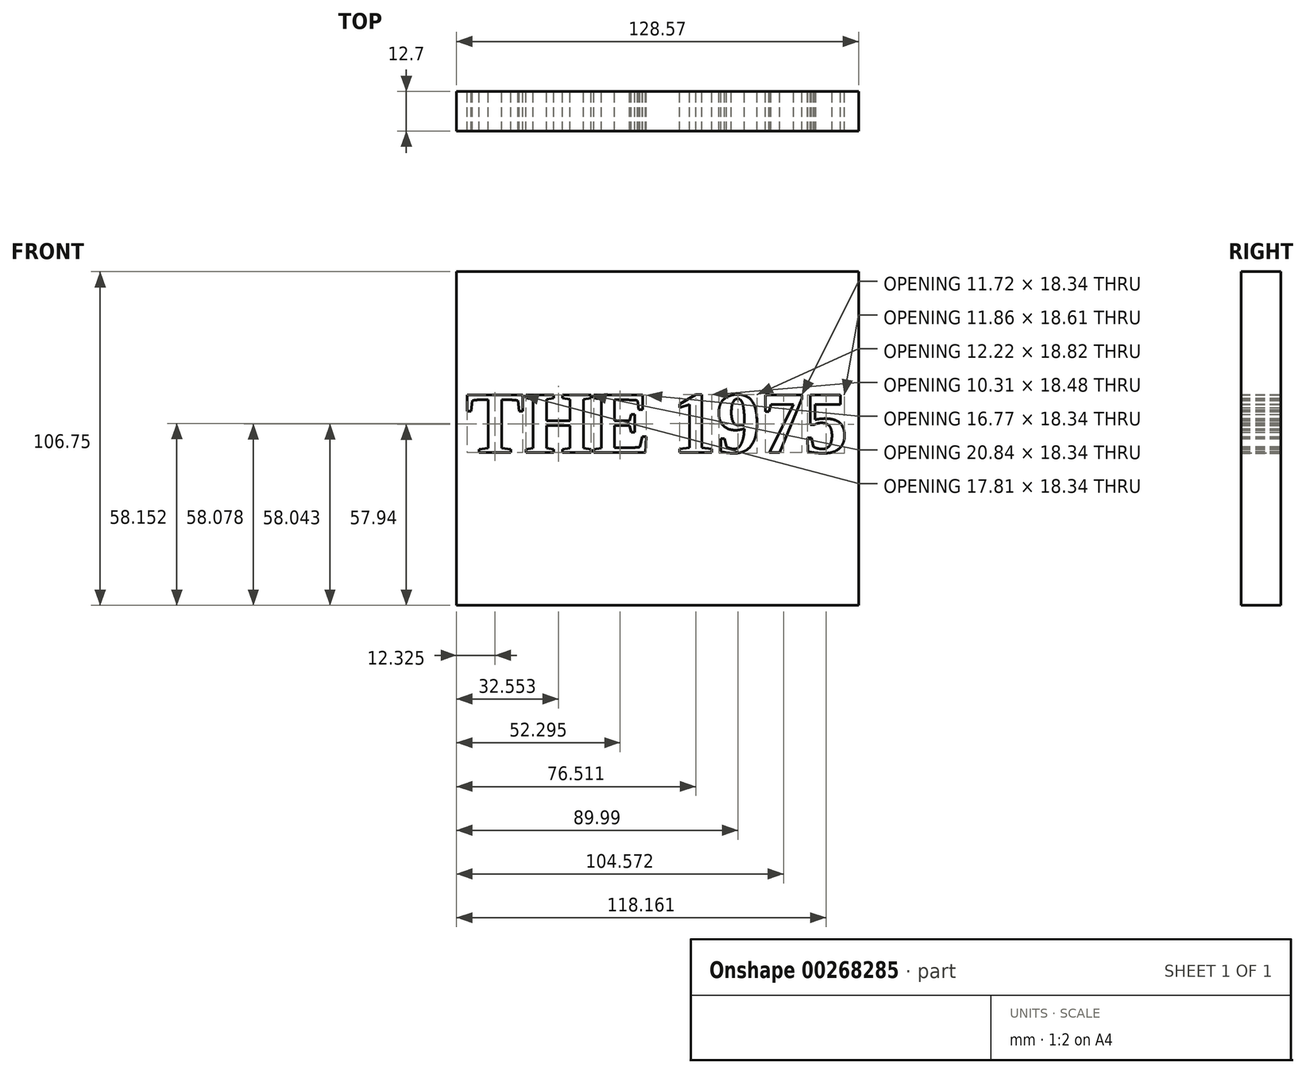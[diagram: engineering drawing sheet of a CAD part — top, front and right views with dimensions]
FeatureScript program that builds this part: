
annotation { "Feature Type Name" : "Feature", "Feature Type Description" : "" }
export const myFeature = defineFeature(function(context is Context, id is Id, definition is map)
    precondition{}
    {
        {
            var Q0;
            Q0=qCreatedBy(makeId("Front.planeOp"),FACE);
            var sketch = newSketch(context, id + "F0", { "sketchPlane" : qUnion([Q0])});
            skLineSegment(sketch, "E0.bottom", {"start": v(-65.7, 50.05) * mm, "end": v(69.14, 50.05) * mm});
            skLineSegment(sketch, "E0.top", {"start": v(-65.7, -64.63) * mm, "end": v(69.14, -64.63) * mm});
            skLineSegment(sketch, "E0.left", {"start": v(-65.7, 50.05) * mm, "end": v(-65.7, -64.63) * mm});
            skLineSegment(sketch, "E0.right", {"start": v(69.14, 50.05) * mm, "end": v(69.14, -64.63) * mm});
            skText(sketch, "E1", { "text": "THE 1975", "fontName": "Tinos-Bold.ttf"});
            skLineSegment(sketch, "E2.bottom", {"start": v(-63.06, 46.42) * mm, "end": v(65.5, 46.42) * mm});
            skLineSegment(sketch, "E2.top", {"start": v(-63.06, -60.33) * mm, "end": v(65.5, -60.33) * mm});
            skLineSegment(sketch, "E2.left", {"start": v(-63.06, 46.42) * mm, "end": v(-63.06, -60.33) * mm});
            skLineSegment(sketch, "E2.right", {"start": v(65.5, 46.42) * mm, "end": v(65.5, -60.33) * mm});
            const initialGuessF0  = {"E1": [-0.06008, -0.01142, 1, 0, 0.02016]};
            skSetInitialGuess(sketch, initialGuessF0);
            skSolve(sketch);
        }
        {
            var Q0;
            Q0=makeQuery(id+"F0.imprint","IMPRINT",FACE,{"disambiguationData":[TD([[makeQuery(id+"F0.imprint","IMPRINT",EDGE,{"derivedFrom":sQuery(id+"F0.wireOp",EDGE,"E1.sketch_text.stroke-0")}),1.0]])]});
            var Q1;
            Q1=makeQuery(id+"F0.imprint","IMPRINT",FACE,{"disambiguationData":[TD([[makeQuery(id+"F0.imprint","IMPRINT",EDGE,{"derivedFrom":sQuery(id+"F0.wireOp",EDGE,"E1.sketch_text.stroke-101")}),1.0]])]});
            extrude(context, id + "F1", {"entities" : qUnion([Q0, Q1]), "depth" : 12.7 * mm});
        }
    });
